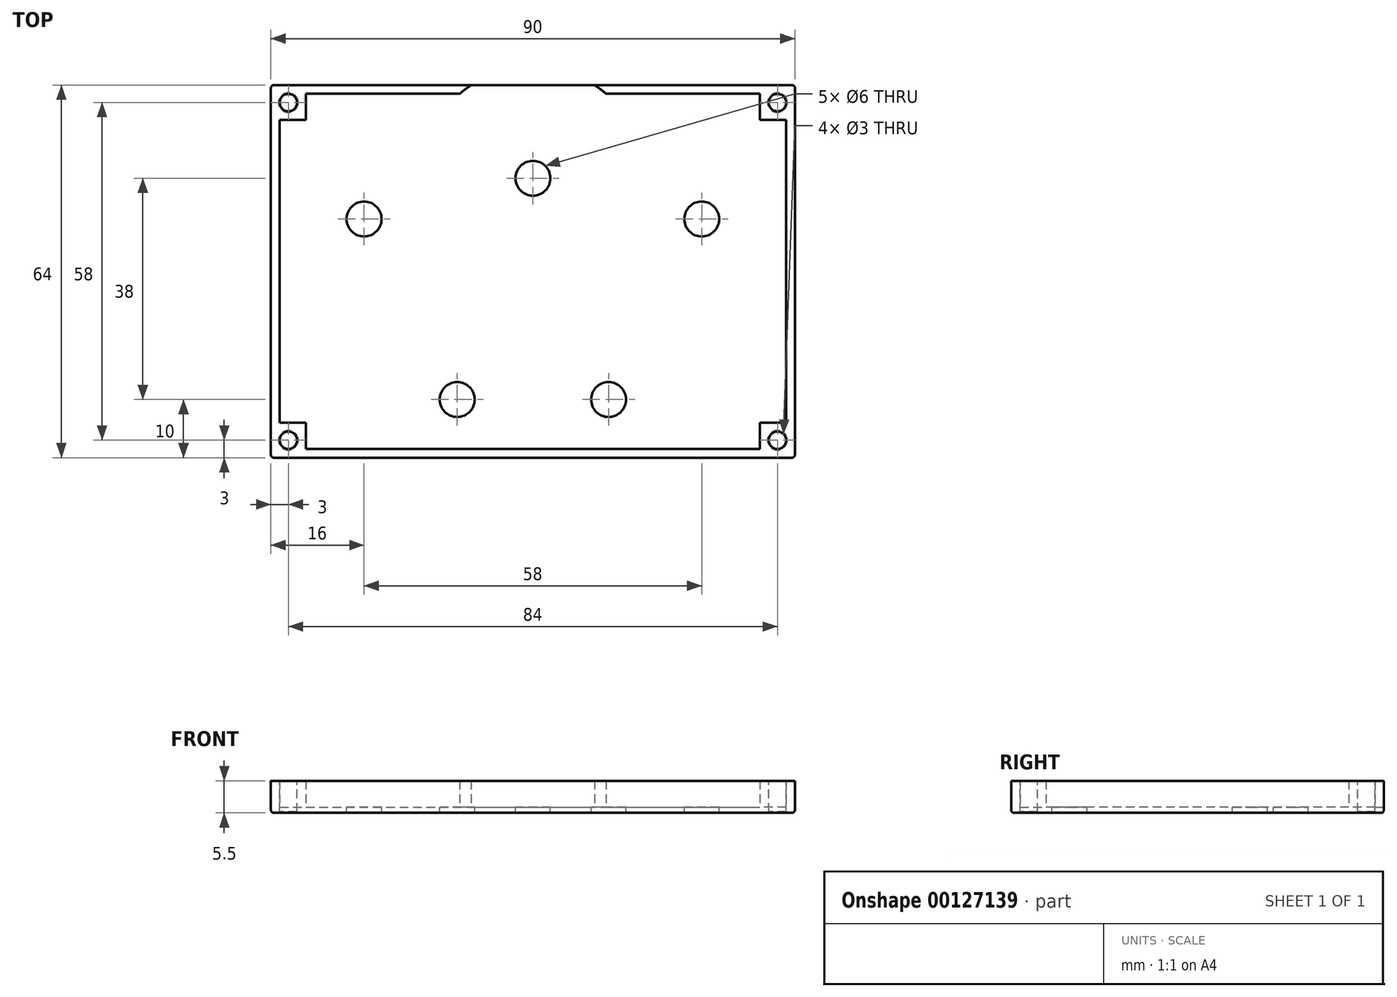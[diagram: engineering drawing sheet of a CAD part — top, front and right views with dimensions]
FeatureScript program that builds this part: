
annotation { "Feature Type Name" : "Feature", "Feature Type Description" : "" }
export const myFeature = defineFeature(function(context is Context, id is Id, definition is map)
    precondition{}
    {
        {
            var Q0;
            Q0=qCreatedBy(makeId("Top.planeOp"),FACE);
            var sketch = newSketch(context, id + "F0", { "sketchPlane" : qUnion([Q0])});
            skLineSegment(sketch, "E0.bottom", {"start": v(0, 0) * mm, "end": v(90, 0) * mm});
            skLineSegment(sketch, "E0.top", {"start": v(0, 64) * mm, "end": v(90, 64) * mm});
            skLineSegment(sketch, "E0.left", {"start": v(0, 0) * mm, "end": v(0, 64) * mm});
            skLineSegment(sketch, "E0.right", {"start": v(90, 0) * mm, "end": v(90, 64) * mm});
            skSolve(sketch);
        }
        {
            var Q0;
            Q0=makeQuery(id+"F0.imprint","IMPRINT",FACE,{"disambiguationData":[TD([[makeQuery(id+"F0.imprint","IMPRINT",EDGE,{"derivedFrom":sQuery(id+"F0.wireOp",EDGE,"E0.bottom")}),1.0]])]});
            extrude(context, id + "F1", {"entities" : qUnion([Q0]), "depth" : 1 * mm});
        }
        {
            var Q0;
            Q0=makeQuery(id+"F1.opExtrude","CAP_FACE",FACE,{"disambiguationData":[OSD([sQuery(id+"F0.wireOp",EDGE,"E0.bottom"),sQuery(id+"F0.wireOp",EDGE,"E0.top"),sQuery(id+"F0.wireOp",EDGE,"E0.left"),sQuery(id+"F0.wireOp",EDGE,"E0.right")])],"isStart":false});
            var sketch = newSketch(context, id + "F2", { "sketchPlane" : qUnion([Q0])});
            skCircle(sketch, "E1", {"center": v(16, 41) * mm, "radius": 18.2 * mm, "construction": true});
            skCircle(sketch, "E2", {"center": v(45, 48) * mm, "radius": 18.2 * mm, "construction": true});
            skCircle(sketch, "E3", {"center": v(74, 41) * mm, "radius": 18.2 * mm, "construction": true});
            skCircle(sketch, "E4", {"center": v(32, 10) * mm, "radius": 12.5 * mm, "construction": true});
            skCircle(sketch, "E5", {"center": v(58, 10) * mm, "radius": 12.5 * mm, "construction": true});
            skLineSegment(sketch, "E6", {"start": v(0, 41) * mm, "end": v(90, 41) * mm, "construction": true});
            skLineSegment(sketch, "E7", {"start": v(45, 64) * mm, "end": v(45, 0) * mm, "construction": true});
            skLineSegment(sketch, "E8", {"start": v(32, 10) * mm, "end": v(58, 10) * mm, "construction": true});
            skPoint(sketch, "E9", {"position": v(45, 10) * mm});
            skSolve(sketch);
        }
        {
            var Q0;
            Q0=makeQuery(id+"F1.opExtrude","CAP_FACE",FACE,{"disambiguationData":[OSD([sQuery(id+"F0.wireOp",EDGE,"E0.bottom"),sQuery(id+"F0.wireOp",EDGE,"E0.top"),sQuery(id+"F0.wireOp",EDGE,"E0.left"),sQuery(id+"F0.wireOp",EDGE,"E0.right")])],"isStart":false});
            var sketch = newSketch(context, id + "F3", { "sketchPlane" : qUnion([Q0])});
            skLineSegment(sketch, "E10.0", {"start": v(0, 0) * mm, "end": v(0, 64) * mm});
            skLineSegment(sketch, "E11.0", {"start": v(0, 64) * mm, "end": v(90, 64) * mm});
            skLineSegment(sketch, "E12.0", {"start": v(90, 0) * mm, "end": v(90, 64) * mm});
            skLineSegment(sketch, "E13.0", {"start": v(0, 0) * mm, "end": v(90, 0) * mm});
            skLineSegment(sketch, "E14.bottom", {"start": v(1.5, 62.5) * mm, "end": v(88.5, 62.5) * mm});
            skLineSegment(sketch, "E14.top", {"start": v(1.5, 1.5) * mm, "end": v(88.5, 1.5) * mm});
            skLineSegment(sketch, "E14.left", {"start": v(1.5, 62.5) * mm, "end": v(1.5, 1.5) * mm});
            skLineSegment(sketch, "E14.right", {"start": v(88.5, 62.5) * mm, "end": v(88.5, 1.5) * mm});
            skSolve(sketch);
        }
        {
            var Q0;
            Q0=makeQuery(id+"F3.imprint","IMPRINT",FACE,{"disambiguationData":[TD([[makeQuery(id+"F3.imprint","IMPRINT",EDGE,{"derivedFrom":sQuery(id+"F3.wireOp",EDGE,"E10.0")}),-1.0]])]});
            extrude(context, id + "F4", {"entities" : qUnion([Q0]), "operationType" : NewBodyOperationType.ADD, "depth" : 4.5 * mm});
        }
        {
            var Q0;
            Q0=makeQuery(id+"F2.imprint","IMPRINT",FACE,{"disambiguationData":[TD([[makeQuery(id+"F2.imprint","IMPRINT",EDGE,{"derivedFrom":makeQuery(id+"F1.opExtrude","CAP_EDGE",EDGE,{"disambiguationData":[OSD([sQuery(id+"F0.wireOp",EDGE,"E0.bottom")])],"isStart":false})}),1.0]])]});
            var sketch = newSketch(context, id + "F5", { "sketchPlane" : qUnion([Q0])});
            skCircle(sketch, "E15", {"center": v(16, 41) * mm, "radius": 3 * mm});
            skCircle(sketch, "E16", {"center": v(45, 48) * mm, "radius": 3 * mm});
            skCircle(sketch, "E17", {"center": v(74, 41) * mm, "radius": 3 * mm});
            skCircle(sketch, "E18", {"center": v(32, 10) * mm, "radius": 3 * mm});
            skCircle(sketch, "E19", {"center": v(58, 10) * mm, "radius": 3 * mm});
            skSolve(sketch);
        }
        {
            var Q0;
            Q0=makeQuery(id+"F5.imprint","IMPRINT",FACE,{"disambiguationData":[TD([[makeQuery(id+"F5.imprint","IMPRINT",EDGE,{"derivedFrom":sQuery(id+"F5.wireOp",EDGE,"E15")}),1.0]])]});
            var Q1;
            Q1=makeQuery(id+"F5.imprint","IMPRINT",FACE,{"disambiguationData":[TD([[makeQuery(id+"F5.imprint","IMPRINT",EDGE,{"derivedFrom":sQuery(id+"F5.wireOp",EDGE,"E16")}),1.0]])]});
            var Q2;
            Q2=makeQuery(id+"F5.imprint","IMPRINT",FACE,{"disambiguationData":[TD([[makeQuery(id+"F5.imprint","IMPRINT",EDGE,{"derivedFrom":sQuery(id+"F5.wireOp",EDGE,"E18")}),1.0]])]});
            var Q3;
            Q3=makeQuery(id+"F5.imprint","IMPRINT",FACE,{"disambiguationData":[TD([[makeQuery(id+"F5.imprint","IMPRINT",EDGE,{"derivedFrom":sQuery(id+"F5.wireOp",EDGE,"E19")}),1.0]])]});
            var Q4;
            Q4=makeQuery(id+"F5.imprint","IMPRINT",FACE,{"disambiguationData":[TD([[makeQuery(id+"F5.imprint","IMPRINT",EDGE,{"derivedFrom":sQuery(id+"F5.wireOp",EDGE,"E17")}),1.0]])]});
            extrude(context, id + "F6", {"entities" : qUnion([Q0, Q1, Q2, Q3, Q4]), "operationType" : NewBodyOperationType.REMOVE, "endBound" : BoundingType.THROUGH_ALL, "oppositeDirection" : true, "depth" : 25 * mm});
        }
        {
            var Q0;
            Q0=makeQuery(id+"F2.imprint","IMPRINT",FACE,{"disambiguationData":[TD([[makeQuery(id+"F2.imprint","IMPRINT",EDGE,{"derivedFrom":makeQuery(id+"F1.opExtrude","CAP_EDGE",EDGE,{"disambiguationData":[OSD([sQuery(id+"F0.wireOp",EDGE,"E0.bottom")])],"isStart":false})}),1.0]])]});
            var sketch = newSketch(context, id + "F7", { "sketchPlane" : qUnion([Q0])});
            skCircle(sketch, "E20.0", {"center": v(45, 48) * mm, "radius": 19.2 * mm});
            skCircle(sketch, "E21.0", {"center": v(32, 10) * mm, "radius": 13.5 * mm});
            skSolve(sketch);
        }
        {
            var Q0;
            {var subQ0=sQuery(id+"F7.wireOp",EDGE,"E20.0");var subQ1=makeQuery(id+"F2.imprint","IMPRINT",EDGE,{"derivedFrom":makeQuery(id+"F1.opExtrude","CAP_EDGE",EDGE,{"disambiguationData":[OSD([sQuery(id+"F0.wireOp",EDGE,"E0.top")])],"isStart":false})});var subQ2=makeQuery(id+"F7.imprint","INTERSECT",VERTEX,{"disambiguationData":[OD(0.0)],"derivedFrom":[subQ1,subQ0]});Q0=makeQuery(id+"F7.imprint","IMPRINT",FACE,{"disambiguationData":[TD([[makeQuery(id+"F7.imprint","IMPRINT",EDGE,{"disambiguationData":[TD([[subQ2,-1.0]])],"derivedFrom":subQ0}),1.0]])]});}
            extrude(context, id + "F8", {"entities" : qUnion([Q0]), "operationType" : NewBodyOperationType.REMOVE, "endBound" : BoundingType.THROUGH_ALL, "depth" : 25 * mm});
        }
        {
            var Q0;
            Q0=makeQuery(id+"F2.imprint","IMPRINT",FACE,{"disambiguationData":[TD([[makeQuery(id+"F2.imprint","IMPRINT",EDGE,{"derivedFrom":makeQuery(id+"F1.opExtrude","CAP_EDGE",EDGE,{"disambiguationData":[OSD([sQuery(id+"F0.wireOp",EDGE,"E0.bottom")])],"isStart":false})}),1.0]])]});
            var sketch = newSketch(context, id + "F9", { "sketchPlane" : qUnion([Q0])});
            skCircle(sketch, "E22.cCircle", {"center": v(16, 41) * mm, "radius": 13.3 * mm, "construction": true});
            skLineSegment(sketch, "E22.0", {"start": v(29.3, 43) * mm, "end": v(29.3, 39) * mm, "construction": true});
            skLineSegment(sketch, "E22.1", {"start": v(29.3, 39) * mm, "end": v(28.12, 35.16) * mm, "construction": true});
            skLineSegment(sketch, "E22.2", {"start": v(28.12, 35.16) * mm, "end": v(25.86, 31.85) * mm, "construction": true});
            skLineSegment(sketch, "E22.3", {"start": v(25.86, 31.85) * mm, "end": v(22.73, 29.35) * mm, "construction": true});
            skLineSegment(sketch, "E22.4", {"start": v(22.73, 29.35) * mm, "end": v(19, 27.89) * mm, "construction": true});
            skLineSegment(sketch, "E22.5", {"start": v(19, 27.89) * mm, "end": v(15, 27.59) * mm, "construction": true});
            skLineSegment(sketch, "E22.6", {"start": v(15, 27.59) * mm, "end": v(11.09, 28.48) * mm, "construction": true});
            skLineSegment(sketch, "E22.7", {"start": v(11.09, 28.48) * mm, "end": v(7.61, 30.48) * mm, "construction": true});
            skLineSegment(sketch, "E22.8", {"start": v(7.61, 30.48) * mm, "end": v(4.89, 33.42) * mm, "construction": true});
            skLineSegment(sketch, "E22.9", {"start": v(4.89, 33.42) * mm, "end": v(3.15, 37.04) * mm, "construction": true});
            skLineSegment(sketch, "E22.10", {"start": v(3.15, 37.04) * mm, "end": v(2.55, 41) * mm, "construction": true});
            skLineSegment(sketch, "E22.11", {"start": v(2.55, 41) * mm, "end": v(3.15, 44.96) * mm, "construction": true});
            skLineSegment(sketch, "E22.12", {"start": v(3.15, 44.96) * mm, "end": v(4.89, 48.58) * mm, "construction": true});
            skLineSegment(sketch, "E22.13", {"start": v(4.89, 48.58) * mm, "end": v(7.61, 51.52) * mm, "construction": true});
            skLineSegment(sketch, "E22.14", {"start": v(7.61, 51.52) * mm, "end": v(11.09, 53.52) * mm, "construction": true});
            skLineSegment(sketch, "E22.15", {"start": v(11.09, 53.52) * mm, "end": v(15, 54.41) * mm, "construction": true});
            skLineSegment(sketch, "E22.16", {"start": v(15, 54.41) * mm, "end": v(19, 54.11) * mm, "construction": true});
            skLineSegment(sketch, "E22.17", {"start": v(19, 54.11) * mm, "end": v(22.73, 52.65) * mm, "construction": true});
            skLineSegment(sketch, "E22.18", {"start": v(22.73, 52.65) * mm, "end": v(25.86, 50.15) * mm, "construction": true});
            skLineSegment(sketch, "E22.19", {"start": v(25.86, 50.15) * mm, "end": v(28.12, 46.84) * mm, "construction": true});
            skLineSegment(sketch, "E22.20", {"start": v(28.12, 46.84) * mm, "end": v(29.3, 43) * mm, "construction": true});
            skPoint(sketch, "E22.0.midPoint", {"position": v(29.3, 41) * mm});
            skCircle(sketch, "E23.cCircle", {"center": v(45, 48) * mm, "radius": 17 * mm, "construction": true});
            skLineSegment(sketch, "E23.0", {"start": v(42.44, 65) * mm, "end": v(47.56, 65) * mm});
            skLineSegment(sketch, "E23.1", {"start": v(47.56, 65) * mm, "end": v(52.46, 63.49) * mm});
            skLineSegment(sketch, "E23.2", {"start": v(52.46, 63.49) * mm, "end": v(56.7, 60.6) * mm});
            skLineSegment(sketch, "E23.3", {"start": v(56.7, 60.6) * mm, "end": v(59.89, 56.6) * mm});
            skLineSegment(sketch, "E23.4", {"start": v(59.89, 56.6) * mm, "end": v(61.76, 51.83) * mm});
            skLineSegment(sketch, "E23.5", {"start": v(61.76, 51.83) * mm, "end": v(62.14, 46.72) * mm});
            skLineSegment(sketch, "E23.6", {"start": v(62.14, 46.72) * mm, "end": v(61, 41.72) * mm});
            skLineSegment(sketch, "E23.7", {"start": v(61, 41.72) * mm, "end": v(58.44, 37.28) * mm});
            skLineSegment(sketch, "E23.8", {"start": v(58.44, 37.28) * mm, "end": v(54.68, 33.8) * mm});
            skLineSegment(sketch, "E23.9", {"start": v(54.68, 33.8) * mm, "end": v(50.07, 31.57) * mm});
            skLineSegment(sketch, "E23.10", {"start": v(50.07, 31.57) * mm, "end": v(45, 30.8) * mm});
            skLineSegment(sketch, "E23.11", {"start": v(45, 30.8) * mm, "end": v(39.93, 31.57) * mm});
            skLineSegment(sketch, "E23.12", {"start": v(39.93, 31.57) * mm, "end": v(35.32, 33.8) * mm});
            skLineSegment(sketch, "E23.13", {"start": v(35.32, 33.8) * mm, "end": v(31.56, 37.28) * mm});
            skLineSegment(sketch, "E23.14", {"start": v(31.56, 37.28) * mm, "end": v(29, 41.72) * mm});
            skLineSegment(sketch, "E23.15", {"start": v(29, 41.72) * mm, "end": v(27.86, 46.72) * mm});
            skLineSegment(sketch, "E23.16", {"start": v(27.86, 46.72) * mm, "end": v(28.24, 51.83) * mm});
            skLineSegment(sketch, "E23.17", {"start": v(28.24, 51.83) * mm, "end": v(30.11, 56.6) * mm});
            skLineSegment(sketch, "E23.18", {"start": v(30.11, 56.6) * mm, "end": v(33.3, 60.6) * mm});
            skLineSegment(sketch, "E23.19", {"start": v(33.3, 60.6) * mm, "end": v(37.54, 63.49) * mm});
            skLineSegment(sketch, "E23.20", {"start": v(37.54, 63.49) * mm, "end": v(42.44, 65) * mm});
            skPoint(sketch, "E23.0.midPoint", {"position": v(45, 65) * mm});
            skLineSegment(sketch, "E24.bottom", {"start": v(42.5, 65) * mm, "end": v(47.5, 65) * mm});
            skLineSegment(sketch, "E24.top", {"start": v(42.5, 62) * mm, "end": v(47.5, 62) * mm});
            skLineSegment(sketch, "E24.left", {"start": v(42.5, 65) * mm, "end": v(42.5, 62) * mm});
            skLineSegment(sketch, "E24.right", {"start": v(47.5, 65) * mm, "end": v(47.5, 62) * mm});
            skLineSegment(sketch, "E25", {"start": v(42.5, 63.5) * mm, "end": v(47.5, 63.5) * mm, "construction": true});
            skLineSegment(sketch, "E26", {"start": v(16, 41) * mm, "end": v(16, 58) * mm, "construction": true});
            skLineSegment(sketch, "E27.bottom", {"start": v(13.5, 58) * mm, "end": v(18.5, 58) * mm});
            skLineSegment(sketch, "E27.top", {"start": v(13.5, 55) * mm, "end": v(18.5, 55) * mm});
            skLineSegment(sketch, "E27.left", {"start": v(13.5, 58) * mm, "end": v(13.5, 55) * mm});
            skLineSegment(sketch, "E27.right", {"start": v(18.5, 58) * mm, "end": v(18.5, 55) * mm});
            skLineSegment(sketch, "E28.MirrorCS", {"start": v(18.5, 58) * mm, "end": v(13.5, 58) * mm});
            skLineSegment(sketch, "E29.MirrorCS", {"start": v(18.5, 55) * mm, "end": v(13.5, 55) * mm});
            skLineSegment(sketch, "E30.0", {"start": v(45, 64) * mm, "end": v(45, 0) * mm, "construction": true});
            skLineSegment(sketch, "E31.MirrorCS", {"start": v(-13, 64) * mm, "end": v(-13, 0) * mm, "construction": true});
            skLineSegment(sketch, "E32.MirrorCS", {"start": v(71.5, 55) * mm, "end": v(76.5, 55) * mm});
            skLineSegment(sketch, "E33.MirrorCS", {"start": v(71.5, 58) * mm, "end": v(71.5, 55) * mm});
            skLineSegment(sketch, "E34.MirrorCS", {"start": v(76.5, 58) * mm, "end": v(76.5, 55) * mm});
            skLineSegment(sketch, "E35.MirrorCS", {"start": v(76.5, 58) * mm, "end": v(71.5, 58) * mm});
            skLineSegment(sketch, "E36.0", {"start": v(32, 10) * mm, "end": v(58, 10) * mm, "construction": true});
            skLineSegment(sketch, "E37", {"start": v(32, 10) * mm, "end": v(32, -0.7) * mm, "construction": true});
            skLineSegment(sketch, "E38.bottom", {"start": v(29.5, 2.3) * mm, "end": v(34.5, 2.3) * mm});
            skLineSegment(sketch, "E38.top", {"start": v(29.5, -0.7) * mm, "end": v(34.5, -0.7) * mm});
            skLineSegment(sketch, "E38.left", {"start": v(29.5, 2.3) * mm, "end": v(29.5, -0.7) * mm});
            skLineSegment(sketch, "E38.right", {"start": v(34.5, 2.3) * mm, "end": v(34.5, -0.7) * mm});
            skLineSegment(sketch, "E39.MirrorCS", {"start": v(60.5, -0.7) * mm, "end": v(55.5, -0.7) * mm});
            skLineSegment(sketch, "E40.MirrorCS", {"start": v(60.5, 2.3) * mm, "end": v(60.5, -0.7) * mm});
            skLineSegment(sketch, "E41.MirrorCS", {"start": v(55.5, 2.3) * mm, "end": v(55.5, -0.7) * mm});
            skLineSegment(sketch, "E42.MirrorCS", {"start": v(60.5, 2.3) * mm, "end": v(55.5, 2.3) * mm});
            skSolve(sketch);
        }
        {
            var Q0;
            Q0=makeQuery(id+"F2.imprint","IMPRINT",FACE,{"disambiguationData":[TD([[makeQuery(id+"F2.imprint","IMPRINT",EDGE,{"derivedFrom":makeQuery(id+"F1.opExtrude","CAP_EDGE",EDGE,{"disambiguationData":[OSD([sQuery(id+"F0.wireOp",EDGE,"E0.bottom")])],"isStart":false})}),1.0]])]});
            var sketch = newSketch(context, id + "F10", { "sketchPlane" : qUnion([Q0])});
            skLineSegment(sketch, "E43.0", {"start": v(45, 64) * mm, "end": v(45, 0) * mm, "construction": true});
            skLineSegment(sketch, "E44.0", {"start": v(90, 0) * mm, "end": v(90, 64) * mm});
            skLineSegment(sketch, "E45", {"start": v(90, 32) * mm, "end": v(0, 32) * mm, "construction": true});
            skLineSegment(sketch, "E46.0", {"start": v(88.5, 62.5) * mm, "end": v(88.5, 1.5) * mm});
            skLineSegment(sketch, "E47.bottom", {"start": v(88.5, 1.5) * mm, "end": v(84, 1.5) * mm});
            skLineSegment(sketch, "E47.top", {"start": v(88.5, 6) * mm, "end": v(84, 6) * mm});
            skLineSegment(sketch, "E47.left", {"start": v(88.5, 1.5) * mm, "end": v(88.5, 6) * mm});
            skLineSegment(sketch, "E47.right", {"start": v(84, 1.5) * mm, "end": v(84, 6) * mm});
            skLineSegment(sketch, "E48.MirrorCS", {"start": v(1.5, 1.5) * mm, "end": v(6, 1.5) * mm});
            skLineSegment(sketch, "E49.MirrorCS", {"start": v(1.5, 1.5) * mm, "end": v(1.5, 6) * mm});
            skLineSegment(sketch, "E50.MirrorCS", {"start": v(1.5, 6) * mm, "end": v(6, 6) * mm});
            skLineSegment(sketch, "E51.MirrorCS", {"start": v(6, 1.5) * mm, "end": v(6, 6) * mm});
            skLineSegment(sketch, "E52.MirrorCS", {"start": v(88.5, 58) * mm, "end": v(84, 58) * mm});
            skLineSegment(sketch, "E53.MirrorCS", {"start": v(84, 62.5) * mm, "end": v(84, 58) * mm});
            skLineSegment(sketch, "E54.MirrorCS", {"start": v(88.5, 62.5) * mm, "end": v(88.5, 58) * mm});
            skLineSegment(sketch, "E55.MirrorCS", {"start": v(88.5, 62.5) * mm, "end": v(84, 62.5) * mm});
            skLineSegment(sketch, "E56.MirrorCS", {"start": v(1.5, 62.5) * mm, "end": v(6, 62.5) * mm});
            skLineSegment(sketch, "E57.MirrorCS", {"start": v(1.5, 58) * mm, "end": v(6, 58) * mm});
            skLineSegment(sketch, "E58.MirrorCS", {"start": v(1.5, 62.5) * mm, "end": v(1.5, 58) * mm});
            skLineSegment(sketch, "E59.MirrorCS", {"start": v(6, 62.5) * mm, "end": v(6, 58) * mm});
            skSolve(sketch);
        }
        {
            var Q0;
            Q0 = qSketchRegion(id + "F10", true);
            var Q1;
            Q1=makeQuery(id+"F4.opExtrude","CAP_FACE",FACE,{"disambiguationData":[OSD([sQuery(id+"F3.wireOp",EDGE,"E10.0"),sQuery(id+"F3.wireOp",EDGE,"E11.0"),sQuery(id+"F3.wireOp",EDGE,"E12.0"),sQuery(id+"F3.wireOp",EDGE,"E13.0"),sQuery(id+"F3.wireOp",EDGE,"E14.bottom"),sQuery(id+"F3.wireOp",EDGE,"E14.top"),sQuery(id+"F3.wireOp",EDGE,"E14.left"),sQuery(id+"F3.wireOp",EDGE,"E14.right")])],"isStart":false});
            extrude(context, id + "F11", {"entities" : qUnion([Q0]), "operationType" : NewBodyOperationType.ADD, "endBound" : BoundingType.UP_TO_SURFACE, "endBoundEntityFace" : qUnion([Q1]), "depth" : 25 * mm});
        }
        {
            var Q0;
            {var subQ0=sQuery(id+"F3.wireOp",EDGE,"E14.right");var subQ1=sQuery(id+"F3.wireOp",EDGE,"E14.left");var subQ2=sQuery(id+"F3.wireOp",EDGE,"E14.top");var subQ3=sQuery(id+"F3.wireOp",EDGE,"E14.bottom");var subQ4=sQuery(id+"F3.wireOp",EDGE,"E13.0");var subQ5=sQuery(id+"F3.wireOp",EDGE,"E12.0");var subQ6=sQuery(id+"F3.wireOp",EDGE,"E11.0");var subQ7=sQuery(id+"F3.wireOp",EDGE,"E10.0");Q0=makeQuery(id+"F11.boolean.opBoolean","MERGE",FACE,{"derivedFrom":[makeQuery(id+"F4.opExtrude","CAP_FACE",FACE,{"disambiguationData":[OSD([subQ7,subQ6,subQ5,subQ4,subQ3,subQ2,subQ1,subQ0])],"isStart":false}),makeQuery(id+"F11.opExtrude","CAP_FACE",FACE,{"disambiguationData":[OSD([subQ7,subQ6,subQ5,subQ4,subQ3,subQ2,subQ1,subQ0]),ownerDisambiguation([makeQuery(id+"F11.opExtrude","SWEPT_BODY",BODY,{"disambiguationData":[OSD([sQuery(id+"F10.wireOp",EDGE,"E47.bottom"),sQuery(id+"F10.wireOp",EDGE,"E47.top"),sQuery(id+"F10.wireOp",EDGE,"E47.left"),sQuery(id+"F10.wireOp",EDGE,"E47.right")])]})])],"isStart":false}),makeQuery(id+"F11.opExtrude","CAP_FACE",FACE,{"disambiguationData":[OSD([subQ7,subQ6,subQ5,subQ4,subQ3,subQ2,subQ1,subQ0]),ownerDisambiguation([makeQuery(id+"F11.opExtrude","SWEPT_BODY",BODY,{"disambiguationData":[OSD([sQuery(id+"F10.wireOp",EDGE,"E48.MirrorCS"),sQuery(id+"F10.wireOp",EDGE,"E49.MirrorCS"),sQuery(id+"F10.wireOp",EDGE,"E50.MirrorCS"),sQuery(id+"F10.wireOp",EDGE,"E51.MirrorCS")])]})])],"isStart":false}),makeQuery(id+"F11.opExtrude","CAP_FACE",FACE,{"disambiguationData":[OSD([subQ7,subQ6,subQ5,subQ4,subQ3,subQ2,subQ1,subQ0]),ownerDisambiguation([makeQuery(id+"F11.opExtrude","SWEPT_BODY",BODY,{"disambiguationData":[OSD([sQuery(id+"F10.wireOp",EDGE,"E52.MirrorCS"),sQuery(id+"F10.wireOp",EDGE,"E53.MirrorCS"),sQuery(id+"F10.wireOp",EDGE,"E54.MirrorCS"),sQuery(id+"F10.wireOp",EDGE,"E55.MirrorCS")])]})])],"isStart":false}),makeQuery(id+"F11.opExtrude","CAP_FACE",FACE,{"disambiguationData":[OSD([subQ7,subQ6,subQ5,subQ4,subQ3,subQ2,subQ1,subQ0]),ownerDisambiguation([makeQuery(id+"F11.opExtrude","SWEPT_BODY",BODY,{"disambiguationData":[OSD([sQuery(id+"F10.wireOp",EDGE,"E56.MirrorCS"),sQuery(id+"F10.wireOp",EDGE,"E57.MirrorCS"),sQuery(id+"F10.wireOp",EDGE,"E58.MirrorCS"),sQuery(id+"F10.wireOp",EDGE,"E59.MirrorCS")])]})])],"isStart":false})]});}
            var sketch = newSketch(context, id + "F12", { "sketchPlane" : qUnion([Q0])});
            skCircle(sketch, "E60", {"center": v(87, 3) * mm, "radius": 1.5 * mm});
            skLineSegment(sketch, "E61.0", {"start": v(90, 32) * mm, "end": v(0, 32) * mm, "construction": true});
            skLineSegment(sketch, "E61.1", {"start": v(45, 64) * mm, "end": v(45, 0) * mm, "construction": true});
            skCircle(sketch, "E62.MirrorC", {"center": v(3, 3) * mm, "radius": 1.5 * mm});
            skCircle(sketch, "E63.MirrorC", {"center": v(87, 61) * mm, "radius": 1.5 * mm});
            skCircle(sketch, "E64.MirrorC", {"center": v(3, 61) * mm, "radius": 1.5 * mm});
            skSolve(sketch);
        }
        {
            var Q0;
            Q0 = qSketchRegion(id + "F12", true);
            extrude(context, id + "F13", {"entities" : qUnion([Q0]), "operationType" : NewBodyOperationType.REMOVE, "endBound" : BoundingType.THROUGH_ALL, "oppositeDirection" : true, "depth" : 25 * mm});
        }
        {
            var Q0;
            {var subQ0=sQuery(id+"F0.wireOp",EDGE,"E0.left");var subQ1=sQuery(id+"F0.wireOp",EDGE,"E0.top");Q0=makeQuery(id+"F0cpSDTWoyvmyJ1_1.boolean.opBoolean","SPLIT",EDGE,{"disambiguationData":[TD([makeQuery(id+"F1.opExtrude","SWEPT_FACE",FACE,{"disambiguationData":[OSD([subQ0])]})])],"derivedFrom":makeQuery(id+"F1.opExtrude","CAP_EDGE",EDGE,{"disambiguationData":[OSD([subQ1])],"isStart":true})});}
            var Q1;
            {var subQ0=sQuery(id+"F0.wireOp",EDGE,"E0.right");var subQ1=sQuery(id+"F0.wireOp",EDGE,"E0.top");Q1=makeQuery(id+"F0cpSDTWoyvmyJ1_1.boolean.opBoolean","SPLIT",EDGE,{"disambiguationData":[TD([makeQuery(id+"F1.opExtrude","SWEPT_FACE",FACE,{"disambiguationData":[OSD([subQ0])]})])],"derivedFrom":makeQuery(id+"F1.opExtrude","CAP_EDGE",EDGE,{"disambiguationData":[OSD([subQ1])],"isStart":true})});}
            var Q2;
            {var subQ0=sQuery(id+"F0.wireOp",EDGE,"E0.bottom");Q2=makeQuery(id+"F0cpSDTWoyvmyJ1_1.boolean.opBoolean","SPLIT",EDGE,{"disambiguationData":[TD([makeQuery(id+"F0cpSDTWoyvmyJ1_1.opExtrude","SWEPT_FACE",FACE,{"disambiguationData":[OSD([sQuery(id+"F9.wireOp",EDGE,"E38.right")])]})])],"derivedFrom":makeQuery(id+"F1.opExtrude","CAP_EDGE",EDGE,{"disambiguationData":[OSD([subQ0])],"isStart":true})});}
            fillet(context, id + "F14", {"entities" : qUnion([Q0, Q1, Q2]), "radius" : 0.5 * mm, "tangentPropagation" : true, "allowEdgeOverflow" : false});
        }
        {
            var Q0;
            Q0=makeQuery(id+"F0cpSDTWoyvmyJ1_1.boolean.opBoolean","COPY",EDGE,{"derivedFrom":makeQuery(id+"F0cpSDTWoyvmyJ1_1.opExtrude","SWEPT_EDGE",EDGE,{"disambiguationData":[OSD([sQuery(id+"F0.wireOp",EDGE,"E0.top"),sQuery(id+"F9.wireOp",EDGE,"E24.left")])]})});
            var Q1;
            Q1=makeQuery(id+"F0cpSDTWoyvmyJ1_1.boolean.opBoolean","COPY",EDGE,{"derivedFrom":makeQuery(id+"F0cpSDTWoyvmyJ1_1.opExtrude","SWEPT_EDGE",EDGE,{"disambiguationData":[OSD([sQuery(id+"F0.wireOp",EDGE,"E0.top"),sQuery(id+"F9.wireOp",EDGE,"E24.right")])]})});
            var Q2;
            Q2=makeQuery(id+"F0cpSDTWoyvmyJ1_1.boolean.opBoolean","INTERSECT",EDGE,{"derivedFrom":[makeQuery(id+"F4.boolean.opBoolean","MERGE",FACE,{"derivedFrom":[makeQuery(id+"F1.opExtrude","SWEPT_FACE",FACE,{"disambiguationData":[OSD([sQuery(id+"F0.wireOp",EDGE,"E0.bottom")])]}),makeQuery(id+"F4.opExtrude","SWEPT_FACE",FACE,{"disambiguationData":[OSD([sQuery(id+"F3.wireOp",EDGE,"E13.0")])]})]}),makeQuery(id+"F0cpSDTWoyvmyJ1_1.opExtrude","SWEPT_FACE",FACE,{"disambiguationData":[OSD([sQuery(id+"F9.wireOp",EDGE,"E40.MirrorCS")])]})]});
            var Q3;
            Q3=makeQuery(id+"F0cpSDTWoyvmyJ1_1.boolean.opBoolean","INTERSECT",EDGE,{"derivedFrom":[makeQuery(id+"F4.boolean.opBoolean","MERGE",FACE,{"derivedFrom":[makeQuery(id+"F1.opExtrude","SWEPT_FACE",FACE,{"disambiguationData":[OSD([sQuery(id+"F0.wireOp",EDGE,"E0.bottom")])]}),makeQuery(id+"F4.opExtrude","SWEPT_FACE",FACE,{"disambiguationData":[OSD([sQuery(id+"F3.wireOp",EDGE,"E13.0")])]})]}),makeQuery(id+"F0cpSDTWoyvmyJ1_1.opExtrude","SWEPT_FACE",FACE,{"disambiguationData":[OSD([sQuery(id+"F9.wireOp",EDGE,"E41.MirrorCS")])]})]});
            var Q4;
            Q4=makeQuery(id+"F0cpSDTWoyvmyJ1_1.boolean.opBoolean","INTERSECT",EDGE,{"derivedFrom":[makeQuery(id+"F4.boolean.opBoolean","MERGE",FACE,{"derivedFrom":[makeQuery(id+"F1.opExtrude","SWEPT_FACE",FACE,{"disambiguationData":[OSD([sQuery(id+"F0.wireOp",EDGE,"E0.bottom")])]}),makeQuery(id+"F4.opExtrude","SWEPT_FACE",FACE,{"disambiguationData":[OSD([sQuery(id+"F3.wireOp",EDGE,"E13.0")])]})]}),makeQuery(id+"F0cpSDTWoyvmyJ1_1.opExtrude","SWEPT_FACE",FACE,{"disambiguationData":[OSD([sQuery(id+"F9.wireOp",EDGE,"E38.right")])]})]});
            var Q5;
            Q5=makeQuery(id+"F0cpSDTWoyvmyJ1_1.boolean.opBoolean","INTERSECT",EDGE,{"derivedFrom":[makeQuery(id+"F4.boolean.opBoolean","MERGE",FACE,{"derivedFrom":[makeQuery(id+"F1.opExtrude","SWEPT_FACE",FACE,{"disambiguationData":[OSD([sQuery(id+"F0.wireOp",EDGE,"E0.bottom")])]}),makeQuery(id+"F4.opExtrude","SWEPT_FACE",FACE,{"disambiguationData":[OSD([sQuery(id+"F3.wireOp",EDGE,"E13.0")])]})]}),makeQuery(id+"F0cpSDTWoyvmyJ1_1.opExtrude","SWEPT_FACE",FACE,{"disambiguationData":[OSD([sQuery(id+"F9.wireOp",EDGE,"E38.left")])]})]});
            var Q6;
            Q6=makeQuery(id+"F4.boolean.opBoolean","MERGE",EDGE,{"derivedFrom":[makeQuery(id+"F1.opExtrude","SWEPT_EDGE",EDGE,{"disambiguationData":[OSD([sQuery(id+"F0.wireOp",EDGE,"E0.bottom"),sQuery(id+"F0.wireOp",EDGE,"E0.left")])]}),makeQuery(id+"F4.opExtrude","SWEPT_EDGE",EDGE,{"disambiguationData":[OSD([sQuery(id+"F3.wireOp",EDGE,"E10.0"),sQuery(id+"F3.wireOp",EDGE,"E13.0")])]})]});
            var Q7;
            Q7=makeQuery(id+"F4.boolean.opBoolean","MERGE",EDGE,{"derivedFrom":[makeQuery(id+"F1.opExtrude","SWEPT_EDGE",EDGE,{"disambiguationData":[OSD([sQuery(id+"F0.wireOp",EDGE,"E0.bottom"),sQuery(id+"F0.wireOp",EDGE,"E0.right")])]}),makeQuery(id+"F4.opExtrude","SWEPT_EDGE",EDGE,{"disambiguationData":[OSD([sQuery(id+"F3.wireOp",EDGE,"E12.0"),sQuery(id+"F3.wireOp",EDGE,"E13.0")])]})]});
            var Q8;
            Q8=makeQuery(id+"F4.boolean.opBoolean","MERGE",EDGE,{"derivedFrom":[makeQuery(id+"F1.opExtrude","SWEPT_EDGE",EDGE,{"disambiguationData":[OSD([sQuery(id+"F0.wireOp",EDGE,"E0.top"),sQuery(id+"F0.wireOp",EDGE,"E0.left")])]}),makeQuery(id+"F4.opExtrude","SWEPT_EDGE",EDGE,{"disambiguationData":[OSD([sQuery(id+"F3.wireOp",EDGE,"E10.0"),sQuery(id+"F3.wireOp",EDGE,"E11.0")])]})]});
            var Q9;
            Q9=makeQuery(id+"F4.boolean.opBoolean","MERGE",EDGE,{"derivedFrom":[makeQuery(id+"F1.opExtrude","SWEPT_EDGE",EDGE,{"disambiguationData":[OSD([sQuery(id+"F0.wireOp",EDGE,"E0.top"),sQuery(id+"F0.wireOp",EDGE,"E0.right")])]}),makeQuery(id+"F4.opExtrude","SWEPT_EDGE",EDGE,{"disambiguationData":[OSD([sQuery(id+"F3.wireOp",EDGE,"E11.0"),sQuery(id+"F3.wireOp",EDGE,"E12.0")])]})]});
            fillet(context, id + "F15", {"entities" : qUnion([Q0, Q1, Q2, Q3, Q4, Q5, Q6, Q7, Q8, Q9]), "radius" : 0.5 * mm, "tangentPropagation" : true, "allowEdgeOverflow" : false});
        }
        {
            var Q0;
            Q0=makeQuery(id+"F13.boolean.opBoolean","INTERSECT",EDGE,{"derivedFrom":[makeQuery(id+"F1.opExtrude","CAP_FACE",FACE,{"disambiguationData":[OSD([sQuery(id+"F0.wireOp",EDGE,"E0.bottom"),sQuery(id+"F0.wireOp",EDGE,"E0.top"),sQuery(id+"F0.wireOp",EDGE,"E0.left"),sQuery(id+"F0.wireOp",EDGE,"E0.right")])],"isStart":true}),makeQuery(id+"F13.opExtrude","SWEPT_FACE",FACE,{"disambiguationData":[OSD([sQuery(id+"F12.wireOp",EDGE,"E63.MirrorC")])]})]});
            var Q1;
            Q1=makeQuery(id+"F13.boolean.opBoolean","INTERSECT",EDGE,{"derivedFrom":[makeQuery(id+"F1.opExtrude","CAP_FACE",FACE,{"disambiguationData":[OSD([sQuery(id+"F0.wireOp",EDGE,"E0.bottom"),sQuery(id+"F0.wireOp",EDGE,"E0.top"),sQuery(id+"F0.wireOp",EDGE,"E0.left"),sQuery(id+"F0.wireOp",EDGE,"E0.right")])],"isStart":true}),makeQuery(id+"F13.opExtrude","SWEPT_FACE",FACE,{"disambiguationData":[OSD([sQuery(id+"F12.wireOp",EDGE,"E60")])]})]});
            var Q2;
            Q2=makeQuery(id+"F13.boolean.opBoolean","INTERSECT",EDGE,{"derivedFrom":[makeQuery(id+"F1.opExtrude","CAP_FACE",FACE,{"disambiguationData":[OSD([sQuery(id+"F0.wireOp",EDGE,"E0.bottom"),sQuery(id+"F0.wireOp",EDGE,"E0.top"),sQuery(id+"F0.wireOp",EDGE,"E0.left"),sQuery(id+"F0.wireOp",EDGE,"E0.right")])],"isStart":true}),makeQuery(id+"F13.opExtrude","SWEPT_FACE",FACE,{"disambiguationData":[OSD([sQuery(id+"F12.wireOp",EDGE,"E62.MirrorC")])]})]});
            var Q3;
            Q3=makeQuery(id+"F13.boolean.opBoolean","INTERSECT",EDGE,{"derivedFrom":[makeQuery(id+"F1.opExtrude","CAP_FACE",FACE,{"disambiguationData":[OSD([sQuery(id+"F0.wireOp",EDGE,"E0.bottom"),sQuery(id+"F0.wireOp",EDGE,"E0.top"),sQuery(id+"F0.wireOp",EDGE,"E0.left"),sQuery(id+"F0.wireOp",EDGE,"E0.right")])],"isStart":true}),makeQuery(id+"F13.opExtrude","SWEPT_FACE",FACE,{"disambiguationData":[OSD([sQuery(id+"F12.wireOp",EDGE,"E64.MirrorC")])]})]});
            chamfer(context, id + "F16", {"entities" : qUnion([Q0, Q1, Q2, Q3]), "width" : 0.2 * mm, "tangentPropagation" : true});
        }
    });
